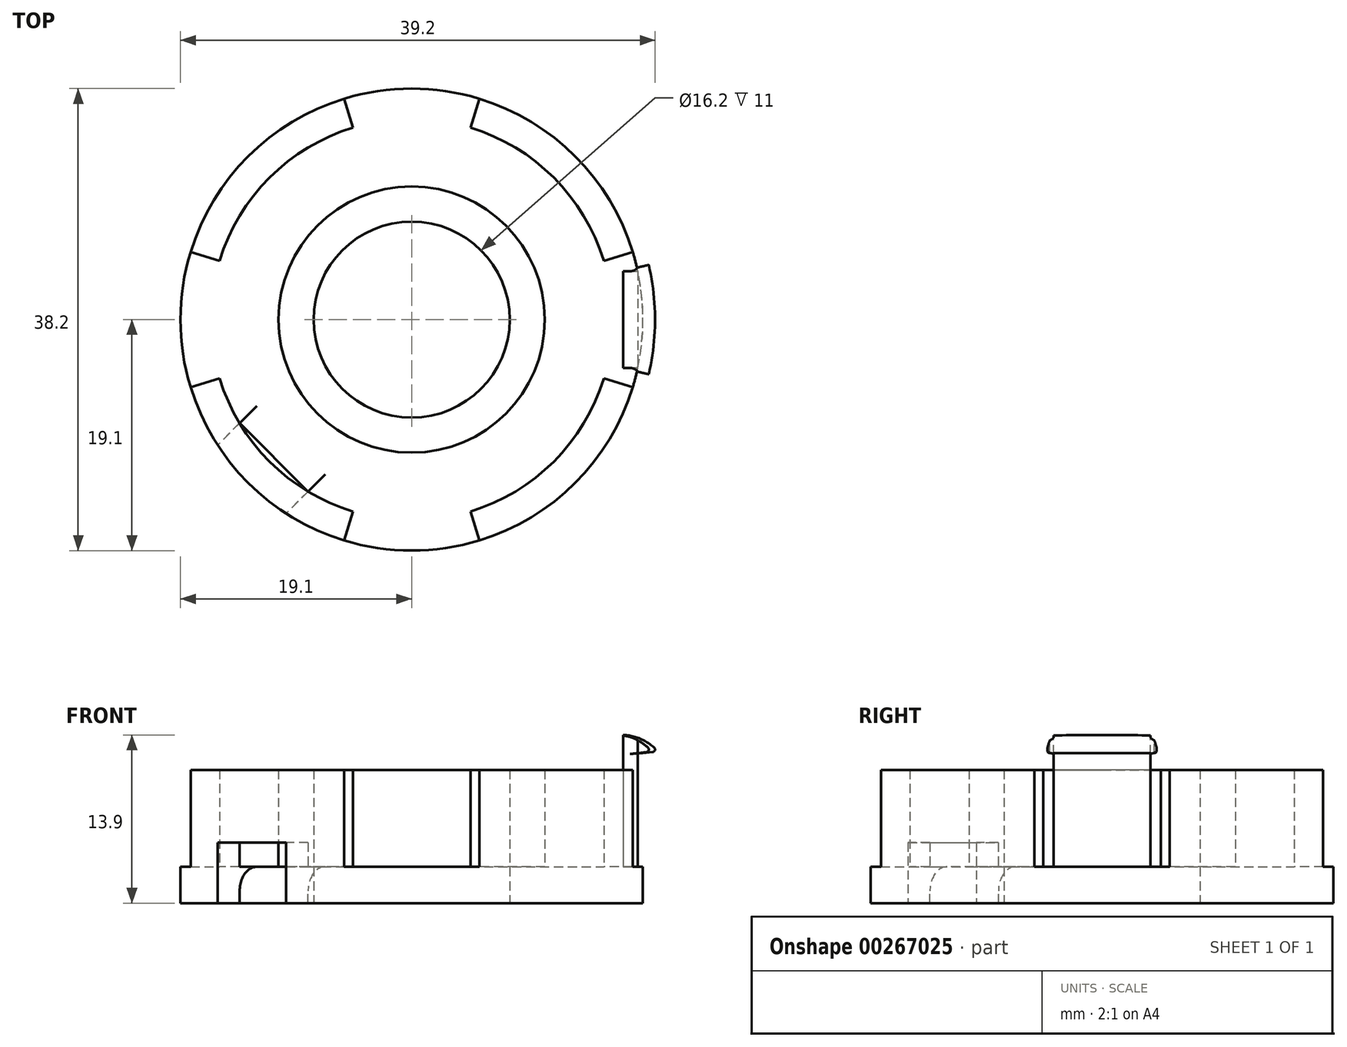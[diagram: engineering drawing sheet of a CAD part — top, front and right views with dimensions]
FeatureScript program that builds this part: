
annotation { "Feature Type Name" : "Feature", "Feature Type Description" : "" }
export const myFeature = defineFeature(function(context is Context, id is Id, definition is map)
    precondition{}
    {
        {
            var Q0;
            Q0=qCreatedBy(makeId("Top.planeOp"),FACE);
            var sketch = newSketch(context, id + "F0", { "sketchPlane" : qUnion([Q0])});
            skCircle(sketch, "E0", {"center": v(0, 0) * mm, "radius": 19.1 * mm});
            skCircle(sketch, "E1", {"center": v(0, 0) * mm, "radius": 8.1 * mm});
            skSolve(sketch);
        }
        {
            var Q0;
            Q0 = qSketchRegion(id + "F0", true);
            extrude(context, id + "F1", {"entities" : qUnion([Q0]), "depth" : 3 * mm, "offsetDistance" : 25 * mm});
        }
        {
            var Q0;
            Q0=makeQuery(id+"F1.opExtrude","CAP_FACE",FACE,{"disambiguationData":[OSD([sQuery(id+"F0.wireOp",EDGE,"E0"),sQuery(id+"F0.wireOp",EDGE,"E1")])],"isStart":false});
            var sketch = newSketch(context, id + "F2", { "sketchPlane" : qUnion([Q0])});
            skLineSegment(sketch, "E2", {"start": v(18.68, 4) * mm, "end": v(18.68, -4) * mm});
            skLineSegment(sketch, "E3", {"start": v(18.68, -4) * mm, "end": v(17.48, -4) * mm});
            skLineSegment(sketch, "E4", {"start": v(17.48, -4) * mm, "end": v(17.48, 4) * mm});
            skLineSegment(sketch, "E5", {"start": v(17.48, 4) * mm, "end": v(18.68, 4) * mm});
            skSolve(sketch);
        }
        {
            var Q0;
            Q0 = qSketchRegion(id + "F2", true);
            extrude(context, id + "F3", {"entities" : qUnion([Q0]), "operationType" : NewBodyOperationType.ADD, "depth" : 10 * mm, "offsetDistance" : 25 * mm});
        }
        {
            var Q0;
            Q0=qCreatedBy(makeId("Front.planeOp"),FACE);
            var sketch = newSketch(context, id + "F4", { "sketchPlane" : qUnion([Q0])});
            skLineSegment(sketch, "E6", {"start": v(17.48, 13.9) * mm, "end": v(17.48, 12.4) * mm});
            skLineSegment(sketch, "E7", {"start": v(17.48, 12.4) * mm, "end": v(19.1, 12.4) * mm});
            skLineSegment(sketch, "E8", {"start": v(19.1, 12.4) * mm, "end": v(19.92, 12.5) * mm});
            skArc(sketch, "E9", {"start": v(19.92, 12.5) * mm, "mid": v(20.1, 12.64) * mm, "end": v(20.04, 12.85) * mm});
            skArc(sketch, "E10", {"start": v(20.04, 12.85) * mm, "mid": v(18.85, 13.6) * mm, "end": v(17.48, 13.9) * mm});
            skLineSegment(sketch, "E11", {"start": v(18.68, 13) * mm, "end": v(18.68, 13.67) * mm, "construction": true});
            skLineSegment(sketch, "E12", {"start": v(14.95, 17.52) * mm, "end": v(26.18, 7.2) * mm, "construction": true});
            skSolve(sketch);
        }
        {
            var Q0;
            Q0 = qSketchRegion(id + "F4", true);
            var Q1;
            Q1=makeQuery(id+"F1.opExtrude","SWEPT_FACE",FACE,{"disambiguationData":[OSD([sQuery(id+"F0.wireOp",EDGE,"E0")])]});
            revolve(context, id + "F5", {"operationType" : NewBodyOperationType.ADD, "entities" : qUnion([Q0]), "axis" : qUnion([Q1]), "revolveType" : RevolveType.TWO_DIRECTIONS, "angle" : 13 * degree, "angleBack" : 347 * degree});
        }
        {
            var Q0;
            {var subQ0=sQuery(id+"F0.wireOp",EDGE,"E1");var subQ1=sQuery(id+"F0.wireOp",EDGE,"E0");var subQ2=makeQuery(id+"F1.opExtrude","CAP_FACE",FACE,{"disambiguationData":[OSD([subQ1,subQ0])],"isStart":false});Q0=makeQuery(id+"F3.boolean.opBoolean","SPLIT",FACE,{"disambiguationData":[TD([makeQuery(id+"F1.opExtrude","SWEPT_FACE",FACE,{"disambiguationData":[OSD([subQ1])]}),subQ2,makeQuery(id+"F1.opExtrude","SWEPT_FACE",FACE,{"disambiguationData":[OSD([subQ0])]}),makeQuery(id+"F3.opExtrude","SWEPT_FACE",FACE,{"disambiguationData":[OSD([sQuery(id+"F2.wireOp",EDGE,"E2")])]}),makeQuery(id+"F3.opExtrude","SWEPT_FACE",FACE,{"disambiguationData":[OSD([sQuery(id+"F2.wireOp",EDGE,"E3")])]}),makeQuery(id+"F3.opExtrude","SWEPT_FACE",FACE,{"disambiguationData":[OSD([sQuery(id+"F2.wireOp",EDGE,"E4")])]}),makeQuery(id+"F3.opExtrude","SWEPT_FACE",FACE,{"disambiguationData":[OSD([sQuery(id+"F2.wireOp",EDGE,"E5")])]})])],"derivedFrom":subQ2});}
            var sketch = newSketch(context, id + "F6", { "sketchPlane" : qUnion([Q0])});
            skLineSegment(sketch, "E13", {"start": v(18.68, -4) * mm, "end": v(18.68, -7) * mm});
            skLineSegment(sketch, "E14", {"start": v(18.68, -7) * mm, "end": v(12.48, -7) * mm});
            skLineSegment(sketch, "E15", {"start": v(12.48, -7) * mm, "end": v(12.48, 7) * mm});
            skLineSegment(sketch, "E16", {"start": v(12.48, 7) * mm, "end": v(18.68, 7) * mm});
            skLineSegment(sketch, "E17", {"start": v(18.68, 7) * mm, "end": v(18.68, 4) * mm});
            skLineSegment(sketch, "E18", {"start": v(18.68, 4) * mm, "end": v(17.48, 4) * mm});
            skLineSegment(sketch, "E19", {"start": v(17.48, 4) * mm, "end": v(17.48, -4) * mm});
            skLineSegment(sketch, "E20", {"start": v(17.48, -4) * mm, "end": v(18.68, -4) * mm});
            skSolve(sketch);
        }
        {
            var Q0;
            Q0 = qSketchRegion(id + "F6", true);
            extrude(context, id + "F7", {"entities" : qUnion([Q0]), "operationType" : NewBodyOperationType.REMOVE, "endBound" : BoundingType.THROUGH_ALL, "depth" : 25 * mm, "offsetDistance" : 25 * mm});
        }
        {
            var Q0;
            Q0=makeQuery(id+"F7.boolean.opBoolean","COPY",EDGE,{"derivedFrom":makeQuery(id+"F7.opExtrude","SWEPT_EDGE",EDGE,{"disambiguationData":[OSD([sQuery(id+"F0.wireOp",EDGE,"E0"),sQuery(id+"F6.wireOp",EDGE,"E13"),sQuery(id+"F6.wireOp",EDGE,"E20")])]})});
            var Q1;
            Q1=makeQuery(id+"F7.boolean.opBoolean","COPY",EDGE,{"derivedFrom":makeQuery(id+"F7.opExtrude","SWEPT_EDGE",EDGE,{"disambiguationData":[OSD([sQuery(id+"F0.wireOp",EDGE,"E0"),sQuery(id+"F6.wireOp",EDGE,"E17"),sQuery(id+"F6.wireOp",EDGE,"E18")])]})});
            var Q2;
            Q2=makeQuery(id+"F3.opExtrude","CAP_EDGE",EDGE,{"disambiguationData":[OSD([sQuery(id+"F2.wireOp",EDGE,"E4")])],"isStart":true});
            fillet(context, id + "F8", {"entities" : qUnion([Q0, Q1, Q2]), "radius" : 0.8 * mm, "tangentPropagation" : true, "allowEdgeOverflow" : false});
        }
        {
            var Q0;
            {var subQ0=sQuery(id+"F2.wireOp",EDGE,"E4");var subQ1=sQuery(id+"F6.wireOp",EDGE,"E20");var subQ2=sQuery(id+"F2.wireOp",EDGE,"E5");var subQ3=makeQuery(id+"FlnYO1eODqvt7H2_1.1.F3.opExtrude","SWEPT_FACE",FACE,{"disambiguationData":[OSD([subQ2])]});var subQ4=sQuery(id+"F6.wireOp",EDGE,"E18");var subQ5=sQuery(id+"F0.wireOp",EDGE,"E1");var subQ6=sQuery(id+"F0.wireOp",EDGE,"E0");var subQ7=makeQuery(id+"F1.opExtrude","CAP_FACE",FACE,{"disambiguationData":[OSD([subQ6,subQ5])],"isStart":false});var subQ8=sQuery(id+"F2.wireOp",EDGE,"E3");var subQ9=makeQuery(id+"FlnYO1eODqvt7H2_1.1.F3.opExtrude","SWEPT_FACE",FACE,{"disambiguationData":[OSD([subQ8])]});var subQ10=makeQuery(id+"FlnYO1eODqvt7H2_1.1.F8.opFillet","BLEND_FACE",FACE,{"disambiguationData":[OSD([subQ0])]});var subQ11=makeQuery(id+"F3.opExtrude","SWEPT_FACE",FACE,{"disambiguationData":[OSD([subQ2])]});var subQ12=makeQuery(id+"FlnYO1eODqvt7H2_1.2.F3.opExtrude","SWEPT_FACE",FACE,{"disambiguationData":[OSD([subQ2])]});var subQ13=makeQuery(id+"FlnYO1eODqvt7H2_1.1.F7.opExtrude","SWEPT_FACE",FACE,{"disambiguationData":[OSD([subQ1])]});var subQ14=sQuery(id+"F2.wireOp",EDGE,"E2");var subQ15=makeQuery(id+"F3.opExtrude","SWEPT_FACE",FACE,{"disambiguationData":[OSD([subQ14])]});var subQ16=makeQuery(id+"F8.opFillet","BLEND_FACE",FACE,{"disambiguationData":[OSD([subQ0])]});var subQ17=makeQuery(id+"FlnYO1eODqvt7H2_1.2.F3.opExtrude","SWEPT_FACE",FACE,{"disambiguationData":[OSD([subQ8])]});var subQ18=makeQuery(id+"FlnYO1eODqvt7H2_1.1.F7.opExtrude","SWEPT_FACE",FACE,{"disambiguationData":[OSD([subQ4])]});var subQ19=makeQuery(id+"F1.opExtrude","SWEPT_FACE",FACE,{"disambiguationData":[OSD([subQ5])]});var subQ20=makeQuery(id+"F7.opExtrude","SWEPT_FACE",FACE,{"disambiguationData":[OSD([subQ1])]});var subQ21=makeQuery(id+"FlnYO1eODqvt7H2_1.2.F3.opExtrude","SWEPT_FACE",FACE,{"disambiguationData":[OSD([subQ14])]});var subQ22=makeQuery(id+"F1.opExtrude","SWEPT_FACE",FACE,{"disambiguationData":[OSD([subQ6])]});var subQ23=makeQuery(id+"F7.opExtrude","SWEPT_FACE",FACE,{"disambiguationData":[OSD([subQ4])]});var subQ24=makeQuery(id+"F3.opExtrude","SWEPT_FACE",FACE,{"disambiguationData":[OSD([subQ8])]});var subQ25=makeQuery(id+"FlnYO1eODqvt7H2_1.1.F3.opExtrude","SWEPT_FACE",FACE,{"disambiguationData":[OSD([subQ14])]});Q0=makeQuery(id+"FlnYO1eODqvt7H2_1.3.F3.boolean.opBoolean","SPLIT",FACE,{"disambiguationData":[TD([subQ22,subQ7,subQ19,subQ15,subQ24,subQ11,subQ23,subQ20,subQ16,subQ25,subQ9,subQ3,subQ18,subQ13,subQ10,subQ21,subQ17,subQ12,makeQuery(id+"FlnYO1eODqvt7H2_1.2.F7.opExtrude","SWEPT_FACE",FACE,{"disambiguationData":[OSD([subQ4])]}),makeQuery(id+"FlnYO1eODqvt7H2_1.2.F7.opExtrude","SWEPT_FACE",FACE,{"disambiguationData":[OSD([subQ1])]}),makeQuery(id+"FlnYO1eODqvt7H2_1.2.F8.opFillet","BLEND_FACE",FACE,{"disambiguationData":[OSD([subQ0])]}),makeQuery(id+"FlnYO1eODqvt7H2_1.3.F3.opExtrude","SWEPT_FACE",FACE,{"disambiguationData":[OSD([subQ14])]}),makeQuery(id+"FlnYO1eODqvt7H2_1.3.F3.opExtrude","SWEPT_FACE",FACE,{"disambiguationData":[OSD([subQ8])]}),makeQuery(id+"FlnYO1eODqvt7H2_1.3.F3.opExtrude","SWEPT_FACE",FACE,{"disambiguationData":[OSD([subQ0])]}),makeQuery(id+"FlnYO1eODqvt7H2_1.3.F3.opExtrude","SWEPT_FACE",FACE,{"disambiguationData":[OSD([subQ2])]})])],"derivedFrom":makeQuery(id+"FlnYO1eODqvt7H2_1.2.F3.boolean.opBoolean","SPLIT",FACE,{"disambiguationData":[TD([subQ22,subQ7,subQ19,subQ15,subQ24,subQ11,subQ23,subQ20,subQ16,subQ25,subQ9,subQ3,subQ18,subQ13,subQ10,subQ21,subQ17,makeQuery(id+"FlnYO1eODqvt7H2_1.2.F3.opExtrude","SWEPT_FACE",FACE,{"disambiguationData":[OSD([subQ0])]}),subQ12])],"derivedFrom":makeQuery(id+"FlnYO1eODqvt7H2_1.1.F3.boolean.opBoolean","SPLIT",FACE,{"disambiguationData":[TD([subQ22,subQ7,subQ19,subQ15,subQ24,subQ11,subQ23,subQ20,subQ16,subQ25,subQ9,makeQuery(id+"FlnYO1eODqvt7H2_1.1.F3.opExtrude","SWEPT_FACE",FACE,{"disambiguationData":[OSD([subQ0])]}),subQ3])],"derivedFrom":makeQuery(id+"F3.boolean.opBoolean","SPLIT",FACE,{"disambiguationData":[TD([subQ22,subQ7,subQ19,subQ15,subQ24,makeQuery(id+"F3.opExtrude","SWEPT_FACE",FACE,{"disambiguationData":[OSD([subQ0])]}),subQ11])],"derivedFrom":subQ7})})})});}
            var sketch = newSketch(context, id + "F9", { "sketchPlane" : qUnion([Q0])});
            skCircle(sketch, "E21", {"center": v(0, 0) * mm, "radius": 8.1 * mm});
            skCircle(sketch, "E22", {"center": v(0, 0) * mm, "radius": 11 * mm});
            skArc(sketch, "E23", {"start": v(-5.58, 18.27) * mm, "mid": v(-13.5, 13.5) * mm, "end": v(-18.27, 5.58) * mm});
            skArc(sketch, "E24", {"start": v(-4.85, 15.87) * mm, "mid": v(-11.74, 11.74) * mm, "end": v(-15.87, 4.85) * mm});
            skLineSegment(sketch, "E25", {"start": v(-18.27, 5.58) * mm, "end": v(-15.87, 4.85) * mm});
            skLineSegment(sketch, "E26", {"start": v(-5.58, 18.27) * mm, "end": v(-4.85, 15.87) * mm});
            skLineSegment(sketch, "E27", {"start": v(-15.87, 4.85) * mm, "end": v(0, 0) * mm, "construction": true});
            skLineSegment(sketch, "E28", {"start": v(-4.85, 15.87) * mm, "end": v(0, 0) * mm, "construction": true});
            skLineSegment(sketch, "E29.MirrorCS", {"start": v(5.58, 18.27) * mm, "end": v(4.85, 15.87) * mm});
            skArc(sketch, "E30.MirrorCS", {"start": v(5.58, 18.27) * mm, "mid": v(13.5, 13.5) * mm, "end": v(18.27, 5.58) * mm});
            skArc(sketch, "E31.MirrorCS", {"start": v(4.85, 15.87) * mm, "mid": v(11.74, 11.74) * mm, "end": v(15.87, 4.85) * mm});
            skLineSegment(sketch, "E32.MirrorCS", {"start": v(18.27, 5.58) * mm, "end": v(15.87, 4.85) * mm});
            skLineSegment(sketch, "E33.MirrorCS", {"start": v(-18.27, -5.58) * mm, "end": v(-15.87, -4.85) * mm});
            skArc(sketch, "E34.MirrorCS", {"start": v(-5.58, -18.27) * mm, "mid": v(-13.5, -13.5) * mm, "end": v(-18.27, -5.58) * mm});
            skArc(sketch, "E35.MirrorCS", {"start": v(-4.85, -15.87) * mm, "mid": v(-11.74, -11.74) * mm, "end": v(-15.87, -4.85) * mm});
            skLineSegment(sketch, "E36.MirrorCS", {"start": v(-5.58, -18.27) * mm, "end": v(-4.85, -15.87) * mm});
            skArc(sketch, "E37.MirrorCS", {"start": v(5.58, -18.27) * mm, "mid": v(13.5, -13.5) * mm, "end": v(18.27, -5.58) * mm});
            skArc(sketch, "E38.MirrorCS", {"start": v(4.85, -15.87) * mm, "mid": v(11.74, -11.74) * mm, "end": v(15.87, -4.85) * mm});
            skLineSegment(sketch, "E39.MirrorCS", {"start": v(5.58, -18.27) * mm, "end": v(4.85, -15.87) * mm});
            skLineSegment(sketch, "E40.MirrorCS", {"start": v(18.27, -5.58) * mm, "end": v(15.87, -4.85) * mm});
            skSolve(sketch);
        }
        {
            var Q0;
            Q0 = qSketchRegion(id + "F9", true);
            extrude(context, id + "F10", {"entities" : qUnion([Q0]), "operationType" : NewBodyOperationType.ADD, "depth" : 8 * mm, "offsetDistance" : 25 * mm});
        }
        {
            var Q0;
            Q0=makeQuery(id+"F10.opExtrude","CAP_FACE",FACE,{"disambiguationData":[OSD([sQuery(id+"F9.wireOp",EDGE,"E33.MirrorCS"),sQuery(id+"F9.wireOp",EDGE,"E34.MirrorCS"),sQuery(id+"F9.wireOp",EDGE,"E35.MirrorCS"),sQuery(id+"F9.wireOp",EDGE,"E36.MirrorCS")])],"isStart":false});
            var sketch = newSketch(context, id + "F11", { "sketchPlane" : qUnion([Q0])});
            skLineSegment(sketch, "E41", {"start": v(-18.27, -5.58) * mm, "end": v(-5.58, -18.27) * mm, "construction": true});
            skLineSegment(sketch, "E42", {"start": v(-19.85, -7.17) * mm, "end": v(-7.17, -19.85) * mm, "construction": true});
            skLineSegment(sketch, "E43", {"start": v(-18.27, -5.58) * mm, "end": v(-19.85, -7.17) * mm, "construction": true});
            skLineSegment(sketch, "E44", {"start": v(-5.58, -18.27) * mm, "end": v(-7.17, -19.85) * mm, "construction": true});
            skSolve(sketch);
        }
        {
            var Q0;
            Q0=sQuery(id+"F11.wireOp",EDGE,"E42");
            cPlane(context, id + "F12", {"entities" : qUnion([Q0]), "cplaneType" : CPlaneType.LINE_ANGLE, "offset" : 25 * mm, "angle" : 270 * degree, "width" : 150 * mm, "height" : 150 * mm});
        }
        {
            var Q0;
            Q0=qCreatedBy(id+"F12.planeOp",FACE);
            var sketch = newSketch(context, id + "F13", { "sketchPlane" : qUnion([Q0])});
            skLineSegment(sketch, "E45.bottom", {"start": v(-4, 0) * mm, "end": v(4, 0) * mm});
            skLineSegment(sketch, "E45.top", {"start": v(-4, 5) * mm, "end": v(4, 5) * mm});
            skLineSegment(sketch, "E45.left", {"start": v(-4, 0) * mm, "end": v(-4, 5) * mm});
            skLineSegment(sketch, "E45.right", {"start": v(4, 0) * mm, "end": v(4, 5) * mm});
            skLineSegment(sketch, "E46", {"start": v(0, 11) * mm, "end": v(0, 0) * mm, "construction": true});
            skSolve(sketch);
        }
        {
            var Q0;
            Q0 = qSketchRegion(id + "F13", true);
            var Q1;
            Q1=sQuery(id+"F13.wireOp",EDGE,"E45.bottom");
            var Q2;
            Q2=sQuery(id+"F13.wireOp",EDGE,"E45.top");
            var Q3;
            Q3=sQuery(id+"F13.wireOp",EDGE,"E45.left");
            var Q4;
            Q4=sQuery(id+"F13.wireOp",EDGE,"E45.right");
            extrude(context, id + "F14", {"entities" : qUnion([Q0]), "operationType" : NewBodyOperationType.REMOVE, "surfaceEntities" : qUnion([Q1, Q2, Q3, Q4]), "oppositeDirection" : true, "depth" : 3 * mm, "offsetDistance" : 25 * mm});
        }
        {
            var Q0;
            {var subQ0=sQuery(id+"F2.wireOp",EDGE,"E4");var subQ1=sQuery(id+"F6.wireOp",EDGE,"E20");var subQ2=sQuery(id+"F2.wireOp",EDGE,"E5");var subQ3=makeQuery(id+"FlnYO1eODqvt7H2_1.1.F3.opExtrude","SWEPT_FACE",FACE,{"disambiguationData":[OSD([subQ2])]});var subQ4=sQuery(id+"F6.wireOp",EDGE,"E18");var subQ5=sQuery(id+"F0.wireOp",EDGE,"E1");var subQ6=sQuery(id+"F0.wireOp",EDGE,"E0");var subQ7=makeQuery(id+"F1.opExtrude","CAP_FACE",FACE,{"disambiguationData":[OSD([subQ6,subQ5])],"isStart":false});var subQ8=sQuery(id+"F2.wireOp",EDGE,"E3");var subQ9=makeQuery(id+"FlnYO1eODqvt7H2_1.1.F3.opExtrude","SWEPT_FACE",FACE,{"disambiguationData":[OSD([subQ8])]});var subQ10=makeQuery(id+"FlnYO1eODqvt7H2_1.1.F8.opFillet","BLEND_FACE",FACE,{"disambiguationData":[OSD([subQ0])]});var subQ11=makeQuery(id+"F3.opExtrude","SWEPT_FACE",FACE,{"disambiguationData":[OSD([subQ2])]});var subQ12=makeQuery(id+"FlnYO1eODqvt7H2_1.2.F3.opExtrude","SWEPT_FACE",FACE,{"disambiguationData":[OSD([subQ2])]});var subQ13=makeQuery(id+"FlnYO1eODqvt7H2_1.1.F7.opExtrude","SWEPT_FACE",FACE,{"disambiguationData":[OSD([subQ1])]});var subQ14=sQuery(id+"F2.wireOp",EDGE,"E2");var subQ15=makeQuery(id+"F3.opExtrude","SWEPT_FACE",FACE,{"disambiguationData":[OSD([subQ14])]});var subQ16=makeQuery(id+"F8.opFillet","BLEND_FACE",FACE,{"disambiguationData":[OSD([subQ0])]});var subQ17=makeQuery(id+"FlnYO1eODqvt7H2_1.2.F3.opExtrude","SWEPT_FACE",FACE,{"disambiguationData":[OSD([subQ8])]});var subQ18=makeQuery(id+"FlnYO1eODqvt7H2_1.1.F7.opExtrude","SWEPT_FACE",FACE,{"disambiguationData":[OSD([subQ4])]});var subQ19=makeQuery(id+"F1.opExtrude","SWEPT_FACE",FACE,{"disambiguationData":[OSD([subQ5])]});var subQ20=makeQuery(id+"F7.opExtrude","SWEPT_FACE",FACE,{"disambiguationData":[OSD([subQ1])]});var subQ21=makeQuery(id+"FlnYO1eODqvt7H2_1.2.F3.opExtrude","SWEPT_FACE",FACE,{"disambiguationData":[OSD([subQ14])]});var subQ22=makeQuery(id+"F1.opExtrude","SWEPT_FACE",FACE,{"disambiguationData":[OSD([subQ6])]});var subQ23=makeQuery(id+"F7.opExtrude","SWEPT_FACE",FACE,{"disambiguationData":[OSD([subQ4])]});var subQ24=makeQuery(id+"F3.opExtrude","SWEPT_FACE",FACE,{"disambiguationData":[OSD([subQ8])]});var subQ25=makeQuery(id+"FlnYO1eODqvt7H2_1.1.F3.opExtrude","SWEPT_FACE",FACE,{"disambiguationData":[OSD([subQ14])]});Q0=makeQuery(id+"F14.boolean.opBoolean","INTERSECT",EDGE,{"derivedFrom":[makeQuery(id+"FlnYO1eODqvt7H2_1.3.F3.boolean.opBoolean","SPLIT",FACE,{"disambiguationData":[TD([subQ22,subQ7,subQ19,subQ15,subQ24,subQ11,subQ23,subQ20,subQ16,subQ25,subQ9,subQ3,subQ18,subQ13,subQ10,subQ21,subQ17,subQ12,makeQuery(id+"FlnYO1eODqvt7H2_1.2.F7.opExtrude","SWEPT_FACE",FACE,{"disambiguationData":[OSD([subQ4])]}),makeQuery(id+"FlnYO1eODqvt7H2_1.2.F7.opExtrude","SWEPT_FACE",FACE,{"disambiguationData":[OSD([subQ1])]}),makeQuery(id+"FlnYO1eODqvt7H2_1.2.F8.opFillet","BLEND_FACE",FACE,{"disambiguationData":[OSD([subQ0])]}),makeQuery(id+"FlnYO1eODqvt7H2_1.3.F3.opExtrude","SWEPT_FACE",FACE,{"disambiguationData":[OSD([subQ14])]}),makeQuery(id+"FlnYO1eODqvt7H2_1.3.F3.opExtrude","SWEPT_FACE",FACE,{"disambiguationData":[OSD([subQ8])]}),makeQuery(id+"FlnYO1eODqvt7H2_1.3.F3.opExtrude","SWEPT_FACE",FACE,{"disambiguationData":[OSD([subQ0])]}),makeQuery(id+"FlnYO1eODqvt7H2_1.3.F3.opExtrude","SWEPT_FACE",FACE,{"disambiguationData":[OSD([subQ2])]})])],"derivedFrom":makeQuery(id+"FlnYO1eODqvt7H2_1.2.F3.boolean.opBoolean","SPLIT",FACE,{"disambiguationData":[TD([subQ22,subQ7,subQ19,subQ15,subQ24,subQ11,subQ23,subQ20,subQ16,subQ25,subQ9,subQ3,subQ18,subQ13,subQ10,subQ21,subQ17,makeQuery(id+"FlnYO1eODqvt7H2_1.2.F3.opExtrude","SWEPT_FACE",FACE,{"disambiguationData":[OSD([subQ0])]}),subQ12])],"derivedFrom":makeQuery(id+"FlnYO1eODqvt7H2_1.1.F3.boolean.opBoolean","SPLIT",FACE,{"disambiguationData":[TD([subQ22,subQ7,subQ19,subQ15,subQ24,subQ11,subQ23,subQ20,subQ16,subQ25,subQ9,makeQuery(id+"FlnYO1eODqvt7H2_1.1.F3.opExtrude","SWEPT_FACE",FACE,{"disambiguationData":[OSD([subQ0])]}),subQ3])],"derivedFrom":makeQuery(id+"F3.boolean.opBoolean","SPLIT",FACE,{"disambiguationData":[TD([subQ22,subQ7,subQ19,subQ15,subQ24,makeQuery(id+"F3.opExtrude","SWEPT_FACE",FACE,{"disambiguationData":[OSD([subQ0])]}),subQ11])],"derivedFrom":subQ7})})})}),makeQuery(id+"F14.opExtrude","CAP_FACE",FACE,{"disambiguationData":[OSD([sQuery(id+"F13.wireOp",EDGE,"E45.bottom"),sQuery(id+"F13.wireOp",EDGE,"E45.top"),sQuery(id+"F13.wireOp",EDGE,"E45.left"),sQuery(id+"F13.wireOp",EDGE,"E45.right")])],"isStart":false})]});}
            fillet(context, id + "F15", {"entities" : qUnion([Q0]), "radius" : 2 * mm, "tangentPropagation" : true, "allowEdgeOverflow" : false});
        }
    });
